# Revit family: PRD_FrankeWS_TltRllHldrs_HEAVYDUTYTripleToiletRollHolder_HDTX675E
name_source: partatom
category: Specialty Equipment
revit_build: Autodesk Revit 2018 (Build: 20190510_1515(x64)
units: mm (PartAtom-declared; Revit-internal decimal feet)

## family parameters
Cut with Voids When Loaded = Yes
Host = Face
OmniClass Number = 23.40.20.21.21
OmniClass Title = Toilet Paper Dispensers
Part Type = Normal
Room Calculation Point = No
Round Connector Dimension = Use Diameter
Shared = No

## types (1)
- HDTX675E
    AssetType = Fixed
    BIMObjectName = PRD_AR_ToiletRollHolders_HEAVYDUTYTripleToiletRollHolder_HDTX675E
    Category = Pr_40_20_76_88, Toilet roll holders
    Default Elevation = 600 mm
    Description = Triple toilet roll holder with spindle system for recessed mounting and re-filling from service room behind the wall, stainless steel, surface satin finished, material thickness 1.5 mm, mounting with stainless steel threaded rods trough the wall, for 3 rolls with max. diameter 120 mm, all 3 rolls accessible from the front, includes stainless steel rods and nuts.
    DurationUnit = year
    Features = stainless steel, surface satin finished
    FillingQuantity = 3
    FillingQuantityUom = Rolls
    Finish = satin finished
    GrossWeight = 7.20 kg
    HolderMaterial = PRD_AR_StainlessSteel_SatinFinished
    IfcExportAs = IfcFurnitureType
    IfcExportType = USERDEFINED
    IntegralAccessories = incl. stainless steel rods and nuts
    IsBuiltIn = TRUE
    MainColor = stainless steel
    Manufacturer = KWC Group AG
    ManufacturerName = KWC Group AG
    ManufacturerURL = www.kwc.com
    Material = stainless steel
    MaterialCode = 1.4301
    MaterialThickness = 1.50 mm
    MaximumDepthDiameterOfConsumable = 120.00 mm
    MaximumWidthOfConsumable = 110.00 mm
    Model = HDTX675E
    ModelNumber = 2000103188
    ModelReference = HDTX675E
    NBSDescription = Toilet roll holders
    NBSReference = 45-35-72/368
    Name = Triple toilet roll holder HDTX675E
    NetWeight = 6.00 kg
    NominalDepth = 174 mm  [stored 0.570866 ft]
    NominalHeight = 498 mm  [stored 1.63386 ft]
    NominalWidth = 240 mm  [stored 0.787402 ft]
    Offset = 0 mm  [stored 0 ft]
    ProductInformation = https://pim.kwc.com
    RollMaterial = PRD_AR_ToiletRoll
    Size = 240 x 498 x 174 mm
    Spindle = Yes
    Style = Roll holder
    TypeOfFixing = Screw
    TypeOfMounting = Recessed mounting
    URL = www.kwc.com
    Uniclass2015Code = Pr_40_20_76_88
    Uniclass2015Title = Toilet roll holders
    Uniclass2015Version = Products v1.17
    Version = 1
    WarrantyDurationUnit = year

note: [stored X ft] marks values corroborated as IEEE doubles in the binary element streams (Revit-internal decimal feet)

## geometry (parser evidence)
native form markers: Sweep x5
no freeform markers — native parametric forms only
